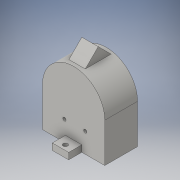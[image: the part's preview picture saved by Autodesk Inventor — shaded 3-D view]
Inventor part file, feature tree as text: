
AUTODESK INVENTOR PART (.ipt)
format: ipt  version: 2016 (Build 200138000, 138)  size: 159,232 bytes
history: native  units: in
note: dims shown in document units (in); Inventor stores cm internally (conversion verified against a paired STEP export)
features: extrude x7, sketch x6, reference x5, plane x1
ambient origin geometry x8: Origin, YZ Plane, XZ Plane, XY Plane, X Axis, Y Axis, Z Axis, Center Point
bodies: Solid1 (feature_tree)
feature tree (19):
  extrude  "Extrusion1"  Depth=0.197in
  extrude  "Extrusion2"  Depth=0.4in
  extrude  "Extrusion3"  Depth=0.4in TaperAngle=0.0deg
  extrude  "Extrusion4"  Depth=0.5in
  extrude  "Extrusion5"  Depth=0.4in TaperAngle=0.0deg
  plane  "Work Plane1"
  extrude  "Extrusion6"  Depth=1.0in
  extrude  "Extrusion7"  Depth=0.4in TaperAngle=0.0deg
  sketch  "Sketch1"  dims[d1=1.0in d2=0.0in d3=0.197in]
  reference  "Reference1"
  reference  "Reference2"
  sketch  "Sketch2"  dims[d4=0.4in d5=0.0in d6=0.15in]
  reference  "Reference3"
  sketch  "Sketch3"  dims[d7=0.1772in d8=0.4in d9=0.0in]
  sketch  "Sketch5"  dims[d10=0.25in d11=0.5in]
  sketch  "Sketch6"  dims[d12=0.197in d13=0.4in d14=0.0in]
  sketch  "Sketch7"  dims[d15=0.15in d16=0.1378in d17=0.4in d18=0.0in d19=0.5in d20=1.9in d21=-0.95in d22=0.1065in d23=0.787in d24=0.394in d25=0.394in d26=0.5in d27=0.0in d28=0.0394in d29=0.098in d30=0.0394in d31=0.098in d32=1.0in d33=0.0in]
  reference  "Reference4"
  reference  "Reference5"
